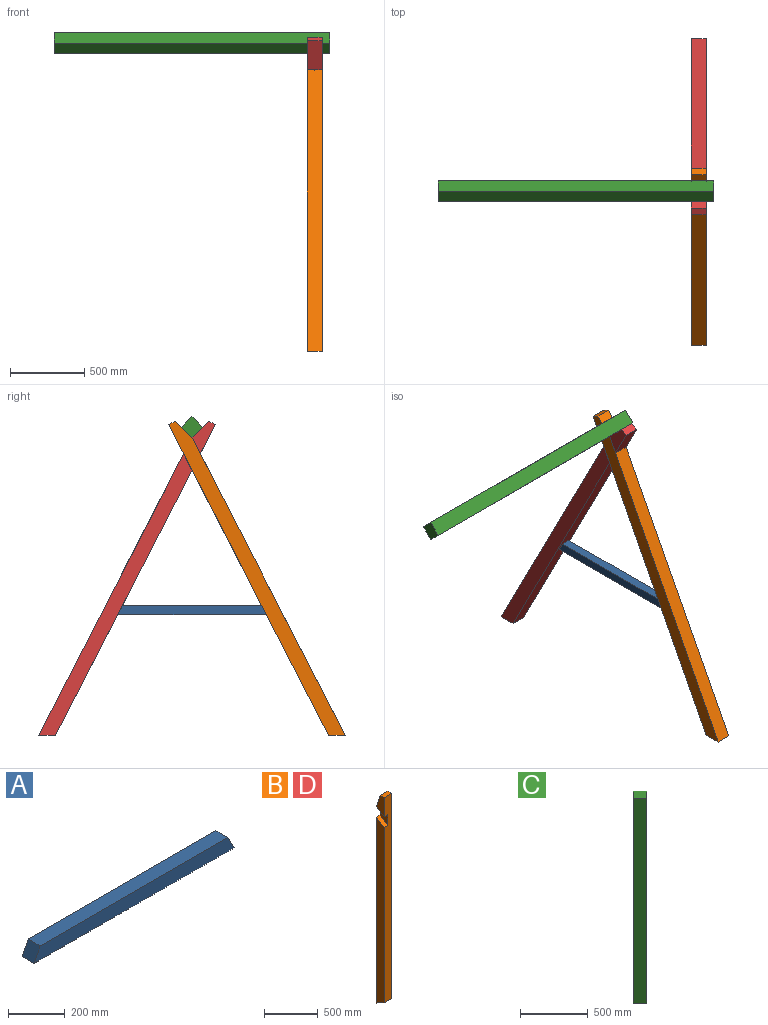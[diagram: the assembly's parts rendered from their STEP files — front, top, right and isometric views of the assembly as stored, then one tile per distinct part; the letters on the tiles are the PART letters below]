
ASSEMBLY  parts=4 mates=3
PART A: 6 faces, bbox 1000x60x60 mm
  f0: plane 938.15x60mm, normal (0,0,1), area 56289.2mm2, adj f1,f2,f4,f5
  f1: plane 1000x60mm, normal (0,-1,0), area 58144.6mm2, adj f0,f3,f4,f5
  f2: plane 1000x60mm, normal (0,1,0), area 58144.6mm2, adj f0,f3,f4,f5
  f3: plane 1000x60mm, normal (0,0,-1), area 60000mm2, adj f1,f2,f4,f5
  f4: plane 60x60mm, normal (0.89,0,0.46), area 4050mm2, adj f0,f1,f2,f3
  f5: plane 60x60mm, normal (-0.89,0,0.46), area 4050mm2, adj f0,f1,f2,f3
PART B: 11 faces, bbox 100x100x2400 mm
  f0: plane 2250x100mm, normal (0,1,0), area 218860.8mm2, adj f2,f3,f7,f8,f9,f10
  f1: plane 100x52.03mm, normal (0,0,1), area 5203.1mm2, adj f3,f4,f5,f10
  f2: plane 2127.22x100mm, normal (-1,0,0), area 206582.4mm2, adj f0,f5,f7,f9
  f3: plane 2400x100mm, normal (1,0,0), area 233825.4mm2, adj f0,f1,f5,f9,f10
  f4: plane 221.25x100mm, normal (-1,0,0), area 14964.6mm2, adj f1,f5,f6,f10
  f5: plane 2348.46x100mm, normal (0,-1,0), area 228706.9mm2, adj f1,f2,f3,f4,f6,f7,f8,f9
  f6: plane 100x71.25mm, normal (0,0.58,-0.81), area 6139.2mm2, adj f4,f5,f8,f10
  f7: plane 100x71.25mm, normal (0,-0.58,0.81), area 6139.2mm2, adj f0,f2,f5,f8
  f8: plane 194.03x100mm, normal (-1,0,0), area 12278.4mm2, adj f0,f5,f6,f7
  f9: plane 100x100mm, normal (0,-0.46,-0.89), area 11250mm2, adj f0,f2,f3,f5
  f10: plane 150x100mm, normal (0,0.95,0.3), area 15748.3mm2, adj f0,f1,f3,f4,f6
PART C: 6 faces, bbox 141.4x141.4x1850 mm
  f0: plane 1850x70.71mm, normal (0.71,0.71,0), area 185000mm2, adj f1,f3,f4,f5
  f1: plane 1850x70.71mm, normal (-0.71,0.71,0), area 185000mm2, adj f0,f2,f4,f5
  f2: plane 1850x70.71mm, normal (-0.71,-0.71,0), area 185000mm2, adj f1,f3,f4,f5
  f3: plane 1850x70.71mm, normal (0.71,-0.71,0), area 185000mm2, adj f0,f2,f4,f5
  f4: plane 141.42x141.42mm, normal (0,0,1), area 10000mm2, adj f0,f1,f2,f3
  f5: plane 141.42x141.42mm, normal (0,0,-1), area 10000mm2, adj f0,f1,f2,f3
PART D: same geometry as B
PLACE A rot(axis=(0,0,1),90deg) t=(-130.67,-0.68,-1230.45)mm
PLACE B rot(axis=(0,0.24,0.97),180deg) t=(-100,-986.33,-2093.62)mm
PLACE C rot(axis=(0,1,0),90deg) t=(-1850,0,0)mm
PLACE D rot(axis=(1,0,0),27.3deg) t=(-100,986.33,-2093.62)mm
MATE fastened A.f5 <-> B.f5  axis (0,-0.89,0.46) through (-100.67,-485.21,-1230.45)mm
MATE fastened B.f10 <-> C.f0  axis (0,-0.71,0.71) through (-50,0,-70.71)mm
MATE fastened D.f10 <-> C.f3  axis (0,0.71,0.71) through (-50,0,-70.71)mm
